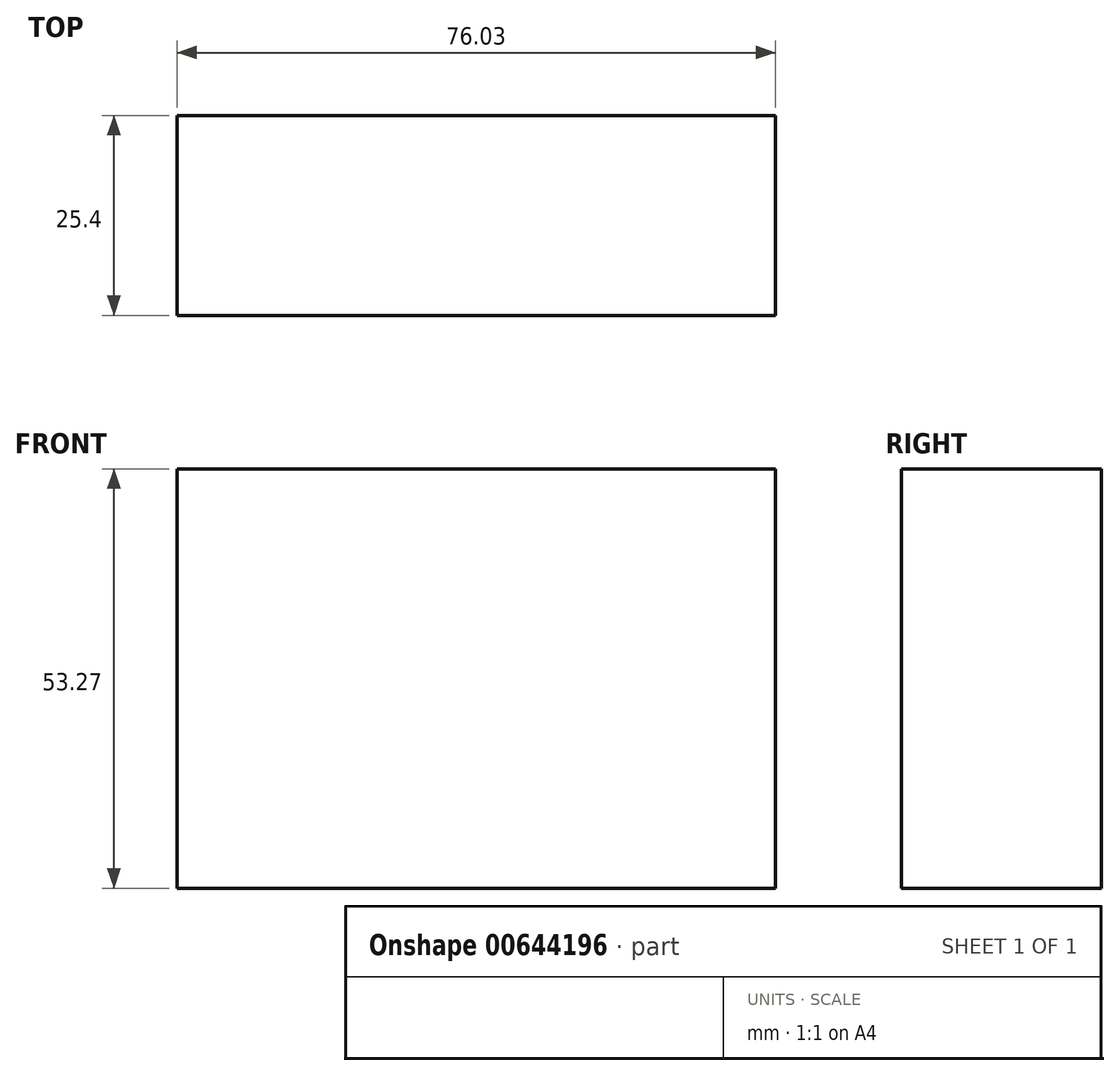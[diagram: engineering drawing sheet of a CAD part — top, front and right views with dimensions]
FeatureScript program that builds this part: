
annotation { "Feature Type Name" : "Feature", "Feature Type Description" : "" }
export const myFeature = defineFeature(function(context is Context, id is Id, definition is map)
    precondition{}
    {
        {
            var Q0;
            Q0=qCreatedBy(makeId("Front.planeOp"),FACE);
            var sketch = newSketch(context, id + "F0", { "sketchPlane" : qUnion([Q0])});
            skLineSegment(sketch, "E0.bottom", {"start": v(0, 0) * mm, "end": v(76.03, 0) * mm});
            skLineSegment(sketch, "E0.top", {"start": v(0, 53.27) * mm, "end": v(76.03, 53.27) * mm});
            skLineSegment(sketch, "E0.left", {"start": v(0, 0) * mm, "end": v(0, 53.27) * mm});
            skLineSegment(sketch, "E0.right", {"start": v(76.03, 0) * mm, "end": v(76.03, 53.27) * mm});
            skSolve(sketch);
        }
        {
            var Q0;
            Q0 = qSketchRegion(id + "F0", true);
            extrude(context, id + "F1", {"entities" : qUnion([Q0]), "depth" : 25.4 * mm, "offsetDistance" : 25.4 * mm});
        }
        {
            var Q0;
            Q0=qCreatedBy(makeId("Front.planeOp"),FACE);
            var sketch = newSketch(context, id + "F2", { "sketchPlane" : qUnion([Q0])});
            skText(sketch, "E1", { "text": "Declan", "fontName": "OpenSans-Regular.ttf"});
            const initialGuessF2  = {"E1": [0.00284, 0.03611, 1, 0, 0.01191]};
            skSetInitialGuess(sketch, initialGuessF2);
            skSolve(sketch);
        }
        {
            var Q0;
            Q0 = qSketchRegion(id + "F2", true);
            extrude(context, id + "F3", {"entities" : qUnion([Q0]), "operationType" : NewBodyOperationType.ADD, "depth" : 25.4 * mm, "offsetDistance" : 25.4 * mm});
        }
    });
